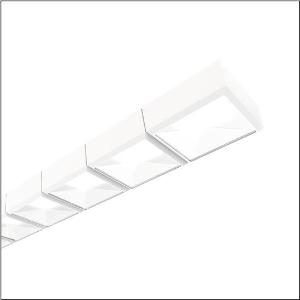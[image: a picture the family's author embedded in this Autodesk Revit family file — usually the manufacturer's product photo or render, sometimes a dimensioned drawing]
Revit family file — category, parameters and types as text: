
# Revit family: scriptus_11_5mz212d03wa
name_source: partatom
category: Lighting Fixtures
units: mm (PartAtom-declared; Revit-internal decimal feet)

## family parameters
Cut with Voids When Loaded = No
Host = Face
Light Source = No
Part Type = Normal
Room Calculation Point = No
Round Connector Dimension = Use Diameter
Shared = No

## types (1)
- Scriptus 11 (1 x LED 3000K / CRI = 80 (unbekannt), 2200 lm, 3000K)
    Apparent Load = 35 VA
    CIE Flux Codes = 82 95 99 100 100
    Color Rendering = 80
    Color Temperature = 3000K
    Default Elevation = 1800 mm
    Description = Scriptus 11, office luminaire, primary optical cover: lenses, CAT 2 (L<= 3000cd/m²), light emission: direct distribution, primary light characteristic: symmetric, installation type: surface-mounted, LED, rated luminous flux: 4.390lm, luminous efficacy: 127lm/W, light colour: 830, colour temperature: 3000K, control gear: DALI, with terminal, 5-pole, mains connection: 230V, AC, 50Hz, rated input power: 35W, housing, luminaire housing, of aluminium, traffic white (RAL 9016), length: 1.658mm, width: 114mm, height: 57mm, protection rating (complete): IP20, insulation class (complete): insulation class I (protective earthing), certification: CE, ENEC, VDE, protection symbol: F, permissible operating ambient temperature: 0..+35°C, standard: EN 50419, packaging unit: 1 piece
    Height = 57 mm
    Lamp = 1 x LED 3000K / CRI >= 80 (unbekannt)
    Lamp Light Flux = 2200 lm
    Lamp count = 1
    Length = 1658 mm
    Luminous efficacy = 127 lm/W
    Manufacturer = Siteco
    ModVariant = No
    Model = 5MZ212D03WA
    Mounting Place = Ceiling
    Mounting Type = Surface mounted
    Number of Poles = 1
    OnlyDefault = Yes
    Power Factor = 1
    Product Name = Scriptus 11
    Product group = office luminaire | ceiling mounted
    ProductGroupID = 301
    Protection Class = Protection class I
    Protection Degree = IP 20
    RLX_Detail_Level = 1
    RLX_Emergency_Light_Flux = 0 lm
    RLX_Emergency_Type = 0
    RLX_Emergency_Type_DB = No
    RlxData = <blob elided: 29409 chars, md5=b3f9388f>
    Socket = socket
    Standby Power = 0 W
    System Light Flux = 4400 lm
    System Power = 35 W
    Type Comments = Product without accessories
    Type Image = l_1004833.jpg
    URL = http://relux.com
    VarID = ---
    Voltage = 0 V
    Weight = 0.00 kg
    Width = 114 mm

## geometry (parser evidence)
native form markers: Blend x4, Sweep x13
no freeform markers — native parametric forms only
